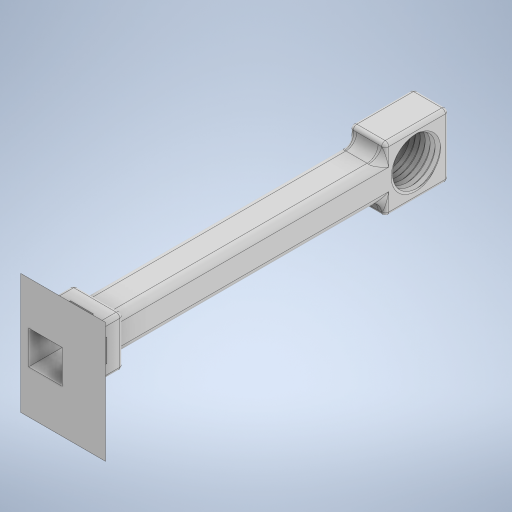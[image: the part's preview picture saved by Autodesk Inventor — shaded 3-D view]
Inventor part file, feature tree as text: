
AUTODESK INVENTOR PART (.ipt)
format: ipt  version: 2024 (Build 280153000, 153)  size: 724,992 bytes
history: native  units: mm
features: sketch x16, extrude x15, fillet x4, mirror x2, other x1
ambient origin geometry x8: Origin, YZ Plane, XZ Plane, XY Plane, X Axis, Y Axis, Z Axis, Center Point
bodies: Volumenkörper1 (feature_tree)
feature tree (38):
  extrude  "Extrusion1"  Depth=10.0mm
  extrude  "Extrusion2"  Depth=10.0mm
  extrude  "Extrusion3"  Depth=18.0mm TaperAngle=0.0deg
  extrude  "Extrusion4"  Depth=9.0mm TaperAngle=0.0deg
  other  "Spirale1"
  extrude  "Extrusion6"  Depth=9.0mm TaperAngle=0.0deg
  extrude  "Extrusion12"  Depth=1.7mm
  mirror  "Spiegeln1"
  extrude  "Extrusion13"  Depth=0.2mm
  mirror  "Spiegeln2"
  extrude  "Extrusion7"  Depth=9.5mm
  extrude  "Extrusion8"  Depth=9.75mm TaperAngle=0.0deg
  extrude  "Extrusion9"  Depth=1.5mm
  extrude  "Extrusion14"  Depth=5.0mm
  extrude  "Extrusion15"  Depth=1.5mm
  extrude  "Extrusion16"  Depth=1.5mm
  extrude  "Extrusion17"  Depth=5.0mm
  extrude  "Extrusion18"  Depth=2.0mm TaperAngle=0.0deg
  fillet  "Rundung3"  Radius=10.0mm
  fillet  "Rundung4"  Radius=15.0mm
  fillet  "Rundung5"  Radius=2.0mm
  fillet  "Rundung6"  Radius=2.0mm
  sketch  "Skizze1"  dims[d0=10.0mm d1=10.0mm]
  sketch  "Skizze2"  dims[d2=91.0mm d3=0.0mm d4=10.0mm]
  sketch  "Skizze3"  dims[d5=18.0mm d6=18.0mm d7=0.0mm]
  sketch  "Skizze4"  dims[d8=15.0mm d9=9.0mm d10=0.0mm]
  sketch  "Skizze5"  dims[d17=12.2mm d18=9.0mm d19=0.0mm]
  sketch  "Skizze7"  dims[d22=1.4mm d23=11.0mm d24=10.0mm d25=0.0mm d26=90.0deg d27=90.0deg d28=0.0mm d29=0.0mm d33=1.7mm]
  sketch  "Skizze8"  dims[d34=60.0deg d35=0.2mm]
  sketch  "Skizze9"  dims[d36=1.0mm d37=0.0mm d39=9.5mm]
  sketch  "Skizze10"  dims[d40=9.5mm d41=9.75mm d42=0.0mm]
  sketch  "Skizze16"  dims[d43=1.5mm d44=1.5mm]
  sketch  "Skizze17"  dims[d45=5.0mm d46=5.0mm]
  sketch  "Skizze18"  dims[d47=1.5mm d48=1.5mm]
  sketch  "Skizze20"  dims[d49=1.5mm d50=1.5mm]
  sketch  "Skizze22"  dims[d51=5.0mm d52=5.0mm]
  sketch  "Skizze23"  dims[d53=1.2mm d54=0.0mm d55=2.0mm d56=0.0mm d65=10.0mm d66=15.0mm d67=2.0mm d68=0.0mm d69=2.0mm d70=0.0mm]
  sketch  "Skizze24"  dims[d71=10.0mm d72=0.0mm d73=10.0mm d74=7.0mm d75=10.0mm d76=24.0mm d77=0.0mm d78=10.0mm d79=24.0mm d80=0.0mm d81=24.0mm d82=0.0mm d83=60.0mm d84=0.0mm d85=10.0mm d86=0.0mm d87=2.0mm d88=1.0mm d89=1.0mm d90=3.1mm d38=0.0mm]
